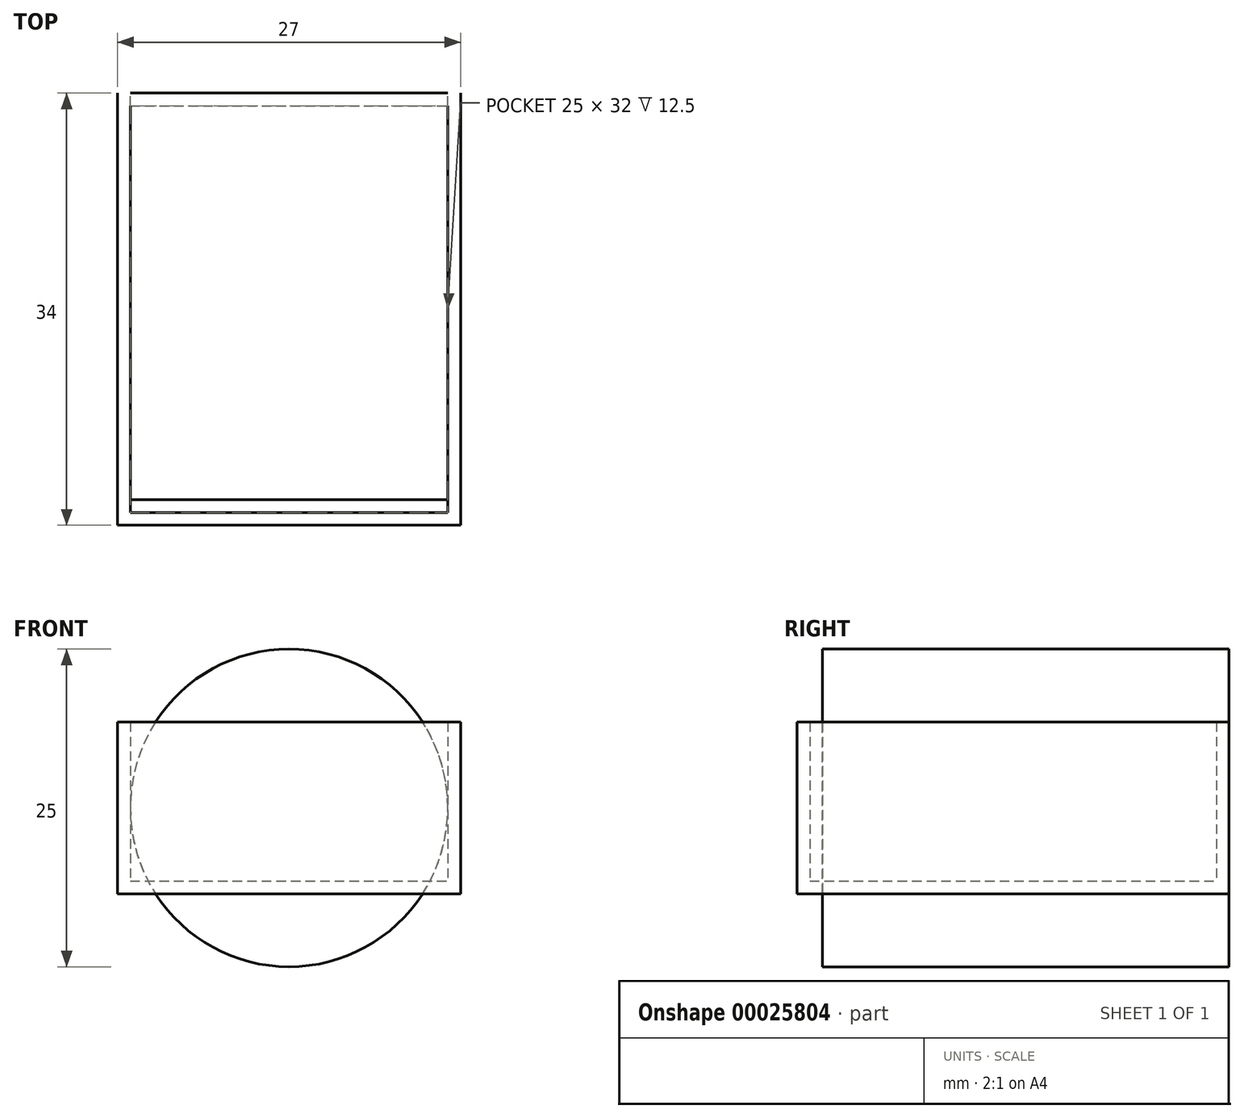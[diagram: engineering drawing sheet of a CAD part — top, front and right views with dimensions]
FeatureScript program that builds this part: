
annotation { "Feature Type Name" : "Feature", "Feature Type Description" : "" }
export const myFeature = defineFeature(function(context is Context, id is Id, definition is map)
    precondition{}
    {
        {
            var Q0;
            Q0=qCreatedBy(makeId("Front.planeOp"),FACE);
            var sketch = newSketch(context, id + "F0", { "sketchPlane" : qUnion([Q0])});
            skCircle(sketch, "E0", {"center": v(0, 0) * mm, "radius": 12.5 * mm});
            skSolve(sketch);
        }
        {
            var Q0;
            Q0 = qSketchRegion(id + "F0", true);
            extrude(context, id + "F1", {"entities" : qUnion([Q0]), "depth" : 32 * mm});
        }
        {
            var Q0;
            Q0=qCreatedBy(makeId("Front.planeOp"),FACE);
            var sketch = newSketch(context, id + "F2", { "sketchPlane" : qUnion([Q0])});
            skLineSegment(sketch, "E1.rect.bottom", {"start": v(-13.5, 6.75) * mm, "end": v(13.5, 6.75) * mm});
            skLineSegment(sketch, "E1.rect.top", {"start": v(-13.5, -6.75) * mm, "end": v(13.5, -6.75) * mm});
            skLineSegment(sketch, "E1.rect.left", {"start": v(-13.5, 6.75) * mm, "end": v(-13.5, -6.75) * mm});
            skLineSegment(sketch, "E1.rect.right", {"start": v(13.5, 6.75) * mm, "end": v(13.5, -6.75) * mm});
            skPoint(sketch, "E1.rect.middle", {"position": v(0, 0) * mm});
            skSolve(sketch);
        }
        {
            var Q0;
            Q0 = qSketchRegion(id + "F2", true);
            extrude(context, id + "F3", {"entities" : qUnion([Q0]), "depth" : 34 * mm});
        }
        {
            var Q0;
            Q0=makeQuery(id+"F3.opExtrude","SWEPT_FACE",FACE,{"disambiguationData":[OSD([sQuery(id+"F2.wireOp",EDGE,"E1.rect.bottom")])]});
            shell(context, id + "F4", {"entities" : qUnion([Q0]), "thickness" : 1 * mm});
        }
    });
